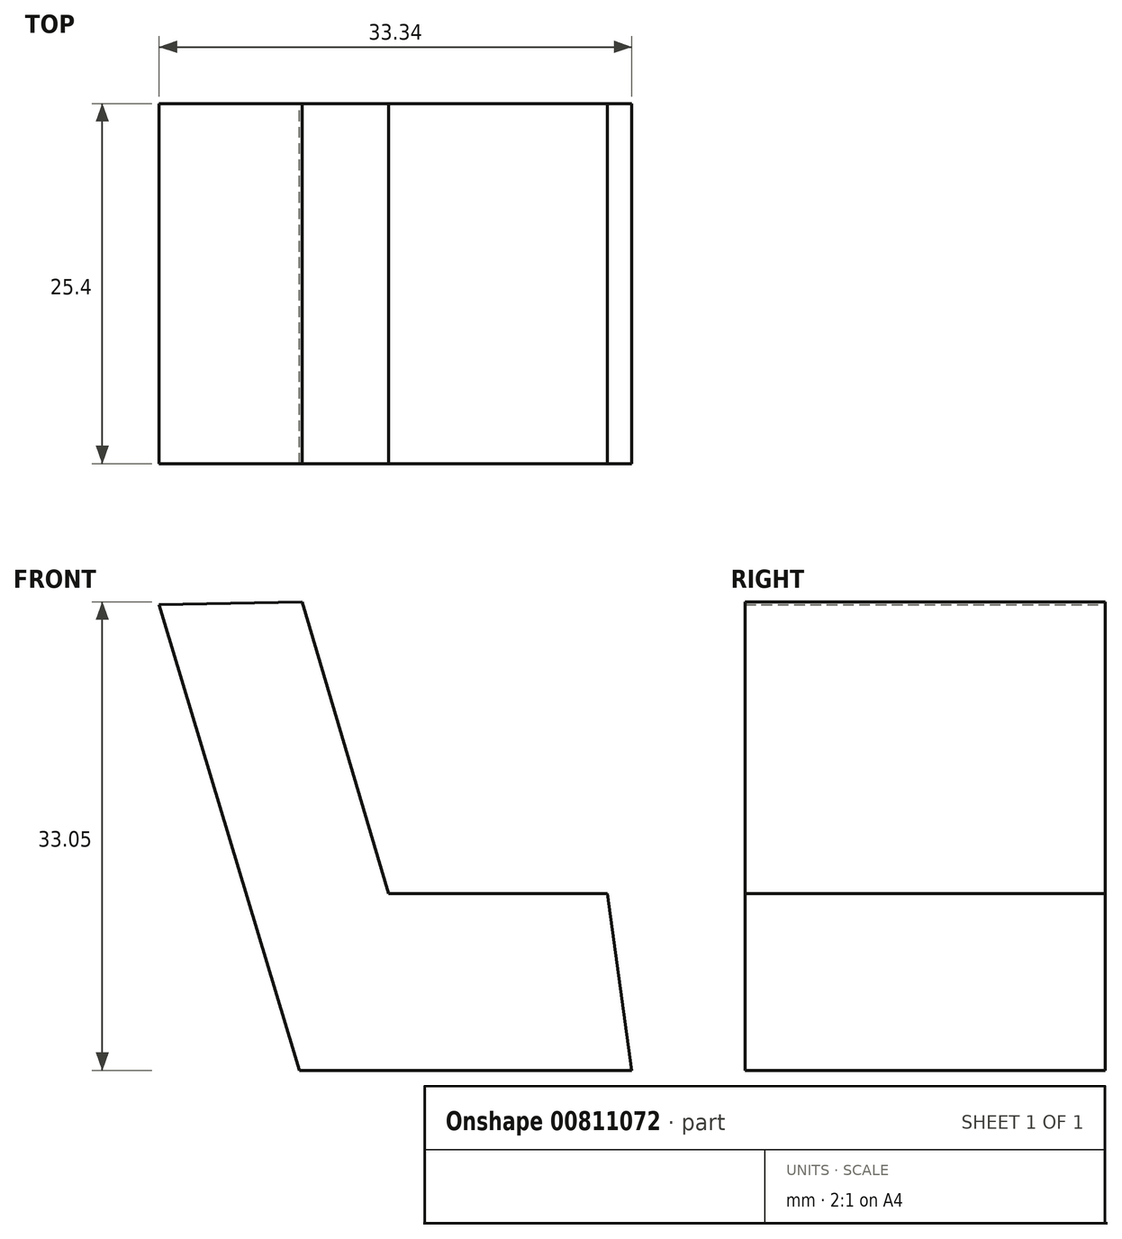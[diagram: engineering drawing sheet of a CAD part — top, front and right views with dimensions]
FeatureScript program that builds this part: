
annotation { "Feature Type Name" : "Feature", "Feature Type Description" : "" }
export const myFeature = defineFeature(function(context is Context, id is Id, definition is map)
    precondition{}
    {
        {
            var Q0;
            Q0=qCreatedBy(makeId("Front.planeOp"),FACE);
            var sketch = newSketch(context, id + "F0", { "sketchPlane" : qUnion([Q0])});
            skLineSegment(sketch, "E0", {"start": v(-14.57, 33.05) * mm, "end": v(-8.48, 12.48) * mm});
            skLineSegment(sketch, "E1", {"start": v(-8.48, 12.48) * mm, "end": v(6.95, 12.48) * mm});
            skLineSegment(sketch, "E2", {"start": v(6.95, 12.48) * mm, "end": v(8.67, 0) * mm});
            skLineSegment(sketch, "E3", {"start": v(8.67, 0) * mm, "end": v(-14.76, 0) * mm});
            skLineSegment(sketch, "E4", {"start": v(-14.76, 0) * mm, "end": v(-24.67, 32.86) * mm});
            skLineSegment(sketch, "E5", {"start": v(-24.67, 32.86) * mm, "end": v(-14.57, 33.05) * mm});
            skSolve(sketch);
        }
        {
            var Q0;
            Q0=makeQuery(id+"F0.imprint","IMPRINT",FACE,{"disambiguationData":[TD([[makeQuery(id+"F0.imprint","IMPRINT",EDGE,{"derivedFrom":sQuery(id+"F0.wireOp",EDGE,"E0")}),-1.0]])]});
            extrude(context, id + "F1", {"entities" : qUnion([Q0]), "depth" : 25.4 * mm, "offsetDistance" : 25.4 * mm});
        }
    });
